# Revit family: 9 Baseboard_HD-Series_End-Cap_SlantFin
name_source: partatom
category: Mechanical Equipment
revit_build: Autodesk Revit 2013 (Build: 20121003_2115(x64)
units: mm (PartAtom-declared; Revit-internal decimal feet)

## types (2) — shared parameters
04 CSI = 23 82 36
95 CSI = 15760
Assembly Code = D3060600
Catalog Sheet URL = http://www.slantfin.com
Color Availability = 9 Colors
Cost Info = http://www.slantfin.com
Default Elevation = 4' - 0"
Installation = http://www.slantfin.com
Installation URL = http://www.slantfin.com
Manufacturer = Slant/Fin Corporation
Manufacturer Fax = (516) 484-5921
Product Page URL = http://www.slantfin.com
Product Selector = http://www.slantfin.com
Product Sheet = http://www.slantfin.com
Product URL = http://www.slantfin.com
Rating Information URL = http://www.slantfin.com
SmartBIM Object Version = 3
Specifications = http://www.slantfin.com
Subcategory = Baseboard Heater
Technical Information = http://www.slantfin.com
URL = http://www.slantfin.com
Unit = Aluminum Satin
Warranty URL = http://www.slantfin.com

## per-type parameters (varying)
| type | Height |
| HD-850 | 0' - 8 1/2" |
| HD-1400 | 1' - 2" |

note: column(s) folded — value = type name in every type: Model

## geometry (parser evidence)
native form markers: Blend x6, Sweep x1
no freeform markers — native parametric forms only
